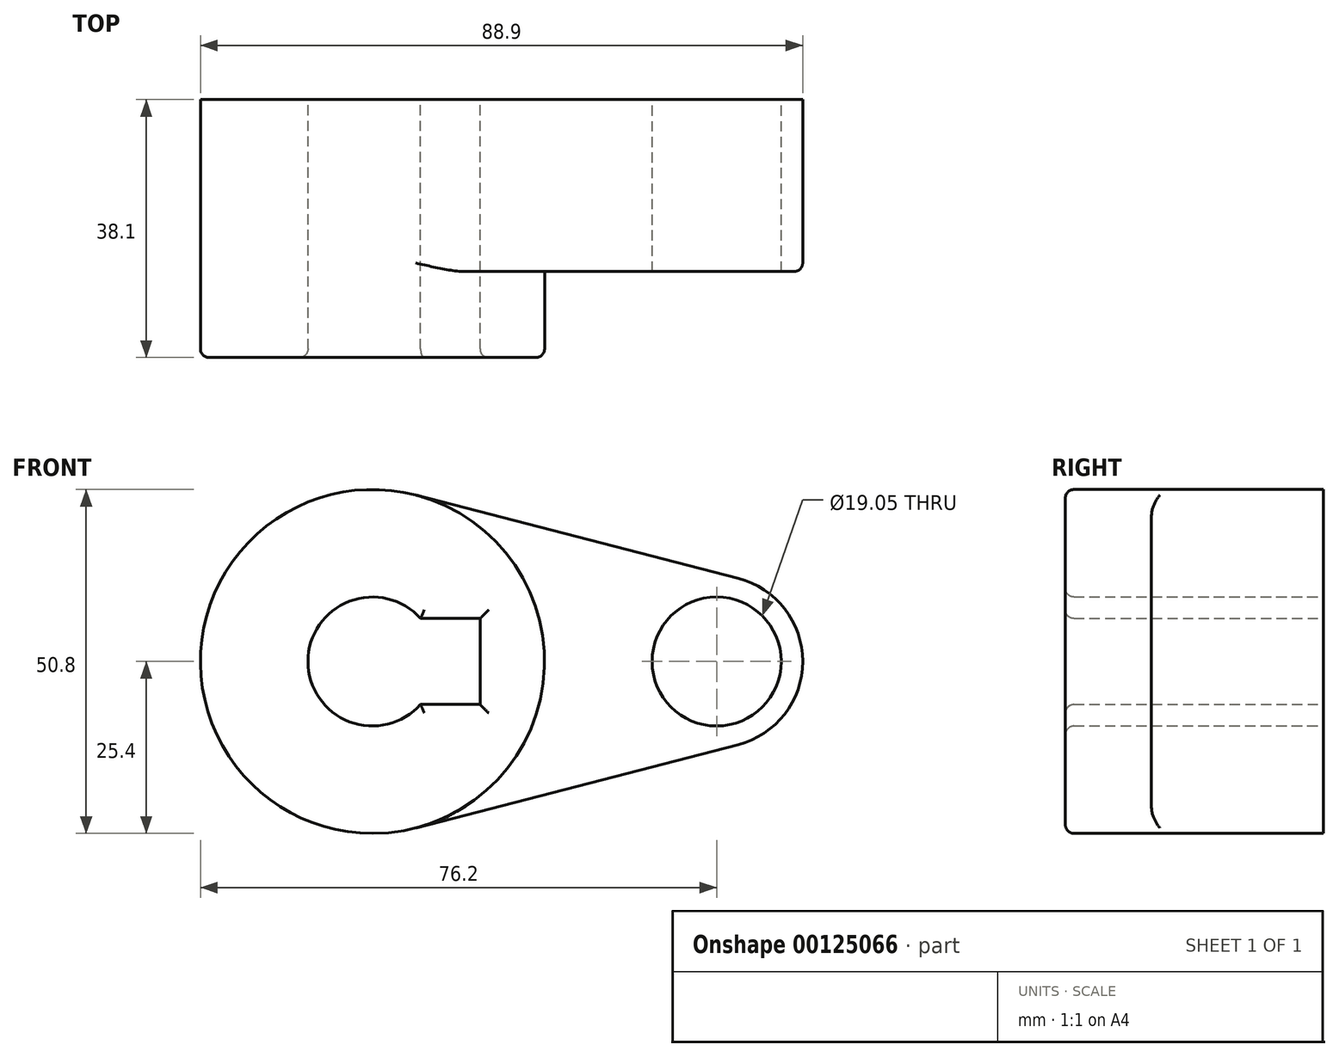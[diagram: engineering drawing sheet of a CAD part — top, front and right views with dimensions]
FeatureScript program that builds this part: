
annotation { "Feature Type Name" : "Feature", "Feature Type Description" : "" }
export const myFeature = defineFeature(function(context is Context, id is Id, definition is map)
    precondition{}
    {
        {
            var Q0;
            Q0=qCreatedBy(makeId("Front.planeOp"),FACE);
            var sketch = newSketch(context, id + "F0", { "sketchPlane" : qUnion([Q0])});
            skCircle(sketch, "E0", {"center": v(0, 0) * mm, "radius": 25.4 * mm});
            skCircle(sketch, "E1", {"center": v(50.8, 0) * mm, "radius": 12.7 * mm});
            skLineSegment(sketch, "E2", {"start": v(6.35, 24.6) * mm, "end": v(53.98, 12.3) * mm});
            skLineSegment(sketch, "E3", {"start": v(6.35, -24.6) * mm, "end": v(53.98, -12.3) * mm});
            skCircle(sketch, "E4", {"center": v(0, 0) * mm, "radius": 9.53 * mm});
            skCircle(sketch, "E5", {"center": v(50.8, 0) * mm, "radius": 9.53 * mm});
            skLineSegment(sketch, "E6.bottom", {"start": v(-15.88, -6.35) * mm, "end": v(15.88, -6.35) * mm});
            skLineSegment(sketch, "E6.top", {"start": v(-15.88, 6.35) * mm, "end": v(15.88, 6.35) * mm});
            skLineSegment(sketch, "E6.left", {"start": v(-15.88, -6.35) * mm, "end": v(-15.88, 6.35) * mm});
            skLineSegment(sketch, "E6.right", {"start": v(15.88, -6.35) * mm, "end": v(15.88, 6.35) * mm});
            skSolve(sketch);
        }
        {
            var Q0;
            {var subQ11=sQuery(id+"F0.wireOp",EDGE,"E6.left");Q0=makeQuery(id+"F0.imprint","IMPRINT",FACE,{"disambiguationData":[TD([[makeQuery(id+"F0.imprint","IMPRINT",EDGE,{"derivedFrom":subQ11}),1.0]])]});}
            var Q1;
            {var subQ5=sQuery(id+"F0.wireOp",EDGE,"E6.left");Q1=makeQuery(id+"F0.imprint","IMPRINT",FACE,{"disambiguationData":[TD([[makeQuery(id+"F0.imprint","IMPRINT",EDGE,{"derivedFrom":subQ5}),-1.0]])]});}
            var Q2;
            {var subQ0=sQuery(id+"F0.wireOp",EDGE,"E2");Q2=makeQuery(id+"F0.imprint","IMPRINT",FACE,{"disambiguationData":[TD([[makeQuery(id+"F0.imprint","IMPRINT",EDGE,{"derivedFrom":subQ0}),-1.0]])]});}
            var Q3;
            Q3=makeQuery(id+"F0.imprint","IMPRINT",FACE,{"disambiguationData":[TD([[makeQuery(id+"F0.imprint","IMPRINT",EDGE,{"derivedFrom":sQuery(id+"F0.wireOp",EDGE,"E5")}),-1.0]])]});
            extrude(context, id + "F1", {"entities" : qUnion([Q0, Q1, Q2, Q3]), "depth" : 25.4 * mm});
        }
        {
            var Q0;
            {var subQ5=sQuery(id+"F0.wireOp",EDGE,"E6.left");Q0=makeQuery(id+"F0.imprint","IMPRINT",FACE,{"disambiguationData":[TD([[makeQuery(id+"F0.imprint","IMPRINT",EDGE,{"derivedFrom":subQ5}),-1.0]])]});}
            var Q1;
            {var subQ11=sQuery(id+"F0.wireOp",EDGE,"E6.left");Q1=makeQuery(id+"F0.imprint","IMPRINT",FACE,{"disambiguationData":[TD([[makeQuery(id+"F0.imprint","IMPRINT",EDGE,{"derivedFrom":subQ11}),1.0]])]});}
            extrude(context, id + "F2", {"entities" : qUnion([Q0, Q1]), "operationType" : NewBodyOperationType.ADD, "depth" : 38.1 * mm});
        }
        {
            var Q0;
            Q0=makeQuery(id+"F2.opExtrude","CAP_EDGE",EDGE,{"disambiguationData":[OSD([sQuery(id+"F0.wireOp",EDGE,"E0")])],"isStart":false});
            fillet(context, id + "F3", {"entities" : qUnion([Q0]), "radius" : 1.27 * mm, "tangentPropagation" : true, "allowEdgeOverflow" : false});
        }
        {
            var Q0;
            Q0=makeQuery(id+"F1.opExtrude","CAP_EDGE",EDGE,{"disambiguationData":[OSD([sQuery(id+"F0.wireOp",EDGE,"E3")])],"isStart":false});
            fillet(context, id + "F4", {"entities" : qUnion([Q0]), "radius" : 1.27 * mm, "tangentPropagation" : true, "allowEdgeOverflow" : false});
        }
        {
            var Q0;
            Q0=makeQuery(id+"F2.opExtrude","CAP_EDGE",EDGE,{"disambiguationData":[OSD([sQuery(id+"F0.wireOp",EDGE,"E6.bottom")])],"isStart":false});
            var Q1;
            Q1=makeQuery(id+"F2.opExtrude","CAP_EDGE",EDGE,{"disambiguationData":[OSD([sQuery(id+"F0.wireOp",EDGE,"E4")])],"isStart":false});
            var Q2;
            Q2=makeQuery(id+"F2.opExtrude","CAP_EDGE",EDGE,{"disambiguationData":[OSD([sQuery(id+"F0.wireOp",EDGE,"E6.top")])],"isStart":false});
            var Q3;
            Q3=makeQuery(id+"F2.opExtrude","CAP_EDGE",EDGE,{"disambiguationData":[OSD([sQuery(id+"F0.wireOp",EDGE,"E6.right")])],"isStart":false});
            fillet(context, id + "F5", {"entities" : qUnion([Q0, Q1, Q2, Q3]), "radius" : 1.27 * mm, "tangentPropagation" : true, "allowEdgeOverflow" : false});
        }
    });
